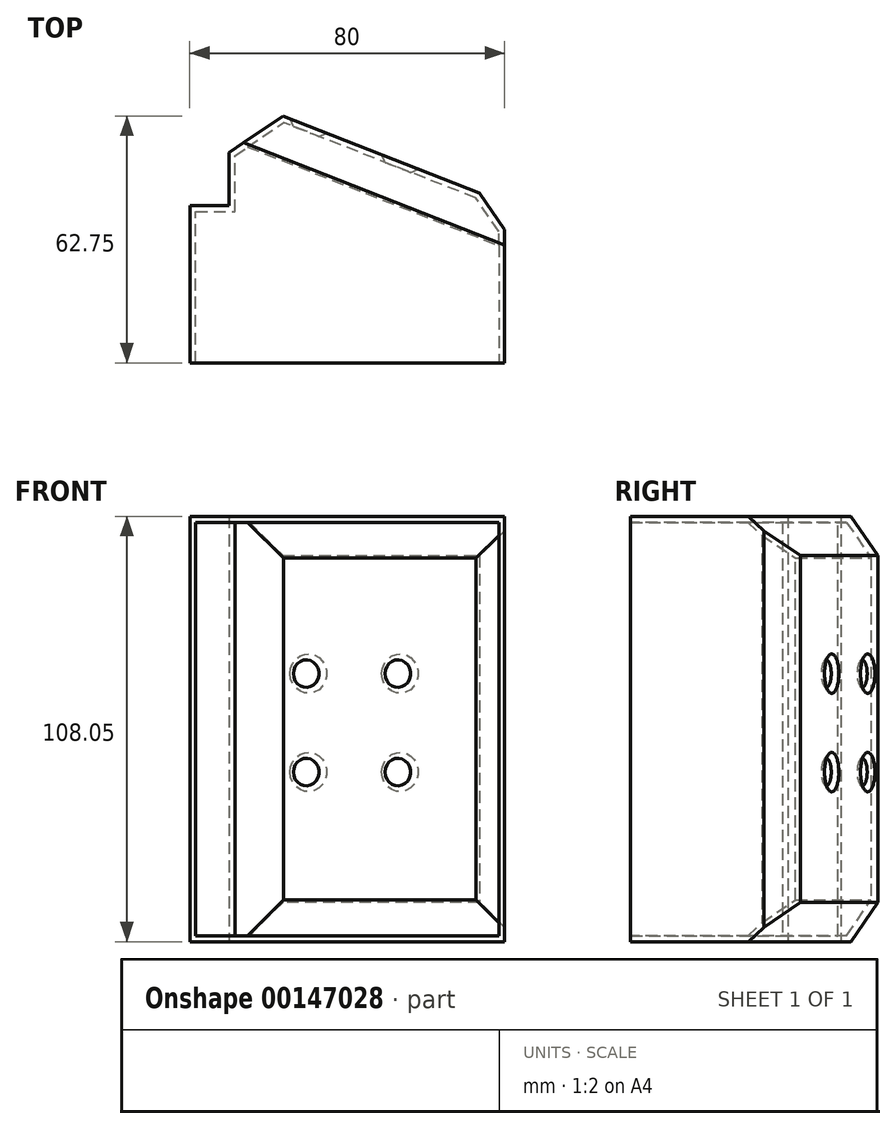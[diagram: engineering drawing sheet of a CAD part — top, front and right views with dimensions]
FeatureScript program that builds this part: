
annotation { "Feature Type Name" : "Feature", "Feature Type Description" : "" }
export const myFeature = defineFeature(function(context is Context, id is Id, definition is map)
    precondition{}
    {
        {
            var Q0;
            Q0=qCreatedBy(makeId("Top.planeOp"),FACE);
            var sketch = newSketch(context, id + "F0", { "sketchPlane" : qUnion([Q0])});
            skLineSegment(sketch, "E0", {"start": v(-53.54, 14.57) * mm, "end": v(16.46, -12.9) * mm});
            skLineSegment(sketch, "E1", {"start": v(16.46, -12.9) * mm, "end": v(16.46, -53.54) * mm});
            skLineSegment(sketch, "E2", {"start": v(16.46, -53.54) * mm, "end": v(-63.54, -53.54) * mm});
            skLineSegment(sketch, "E3", {"start": v(-63.54, -53.54) * mm, "end": v(-63.54, -13.54) * mm});
            skLineSegment(sketch, "E4", {"start": v(-63.54, -13.54) * mm, "end": v(-53.54, -13.54) * mm});
            skLineSegment(sketch, "E5", {"start": v(-53.54, -13.54) * mm, "end": v(-53.54, 14.57) * mm});
            skSolve(sketch);
        }
        {
            var Q0;
            Q0=makeQuery(id+"F0.imprint","IMPRINT",FACE,{"disambiguationData":[TD([[makeQuery(id+"F0.imprint","IMPRINT",EDGE,{"derivedFrom":sQuery(id+"F0.wireOp",EDGE,"E0")}),-1.0]])]});
            extrude(context, id + "F1", {"entities" : qUnion([Q0]), "depth" : 108.05 * mm});
        }
        {
            var Q0;
            Q0=makeQuery(id+"F1.opExtrude","SWEPT_FACE",FACE,{"disambiguationData":[OSD([sQuery(id+"F0.wireOp",EDGE,"E0")])]});
            chamfer(context, id + "F2", {"entities" : qUnion([Q0]), "width" : 10 * mm, "tangentPropagation" : true});
        }
        {
            var Q0;
            Q0=makeQuery(id+"F1.opExtrude","SWEPT_FACE",FACE,{"disambiguationData":[OSD([sQuery(id+"F0.wireOp",EDGE,"E0")])]});
            var sketch = newSketch(context, id + "F3", { "sketchPlane" : qUnion([Q0])});
            skSolve(sketch);
        }
        {
            var Q0;
            Q0=makeQuery(id+"F1.opExtrude","SWEPT_FACE",FACE,{"disambiguationData":[OSD([sQuery(id+"F0.wireOp",EDGE,"E2")])]});
            var Q1;
            Q1=makeQuery(id+"F1.opExtrude","SWEPT_BODY",BODY,{"disambiguationData":[OSD([sQuery(id+"F0.wireOp",EDGE,"E0"),sQuery(id+"F0.wireOp",EDGE,"E1"),sQuery(id+"F0.wireOp",EDGE,"E2"),sQuery(id+"F0.wireOp",EDGE,"E3"),sQuery(id+"F0.wireOp",EDGE,"E4"),sQuery(id+"F0.wireOp",EDGE,"E5")])]});
            shell(context, id + "F4", {"entities" : qUnion([Q0]), "parts" : qUnion([Q1]), "thickness" : 1.5 * mm});
        }
        {
            var Q0;
            {var subQ0=sQuery(id+"F0.wireOp",EDGE,"E0");var subQ1=makeQuery(id+"F1.opExtrude","SWEPT_FACE",FACE,{"disambiguationData":[OSD([subQ0])]});Q0=makeQuery(id+"F3.imprint","IMPRINT",FACE,{"disambiguationData":[TD([[makeQuery(id+"F3.imprint","IMPRINT",EDGE,{"derivedFrom":makeQuery(id+"F2.opChamfer","BLEND_EDGE",EDGE,{"blendedFrom":[makeQuery(id+"F1.opExtrude","CAP_EDGE",EDGE,{"disambiguationData":[OSD([subQ0])],"isStart":true}),subQ1],"blendedInto":[subQ1]})}),1.0]])]});}
            var sketch = newSketch(context, id + "F5", { "sketchPlane" : qUnion([Q0])});
            skPoint(sketch, "E6", {"position": v(8.54, 43.09) * mm});
            skPoint(sketch, "E7.0.1.0", {"position": v(8.54, 68.09) * mm});
            skPoint(sketch, "E7.1.0.0", {"position": v(33.54, 43.09) * mm});
            skPoint(sketch, "E7.1.1.0", {"position": v(33.54, 68.09) * mm});
            skLineSegment(sketch, "E7.direction1", {"start": v(8.54, 43.09) * mm, "end": v(33.54, 43.09) * mm, "construction": true});
            skLineSegment(sketch, "E7.direction2", {"start": v(8.54, 43.09) * mm, "end": v(8.54, 68.09) * mm, "construction": true});
            skSolve(sketch);
        }
        {
            var Q0;
            Q0=sQuery(id+"F5.wireOp",VERTEX,"E7.1.1.0");
            var Q1;
            Q1=sQuery(id+"F5.wireOp",VERTEX,"E7.1.0.0");
            var Q2;
            Q2=sQuery(id+"F5.wireOp",VERTEX,"E6");
            var Q3;
            Q3=sQuery(id+"F5.wireOp",VERTEX,"E7.0.1.0");
            var Q4;
            Q4=makeQuery(id+"F1.opExtrude","SWEPT_BODY",BODY,{"disambiguationData":[OSD([sQuery(id+"F0.wireOp",EDGE,"E0"),sQuery(id+"F0.wireOp",EDGE,"E1"),sQuery(id+"F0.wireOp",EDGE,"E2"),sQuery(id+"F0.wireOp",EDGE,"E3"),sQuery(id+"F0.wireOp",EDGE,"E4"),sQuery(id+"F0.wireOp",EDGE,"E5")])]});
            hole(context, id + "F6", {"style" : HoleStyle.C_SINK, "endStyle" : HoleEndStyle.THROUGH, "holeDiameter" : 5 * mm, "cSinkDiameter" : 10 * mm, "cSinkAngle" : 90 * degree, "locations" : qUnion([Q0, Q1, Q2, Q3]), "scope" : qUnion([Q4]), "isTappedThrough" : true});
        }
    });
